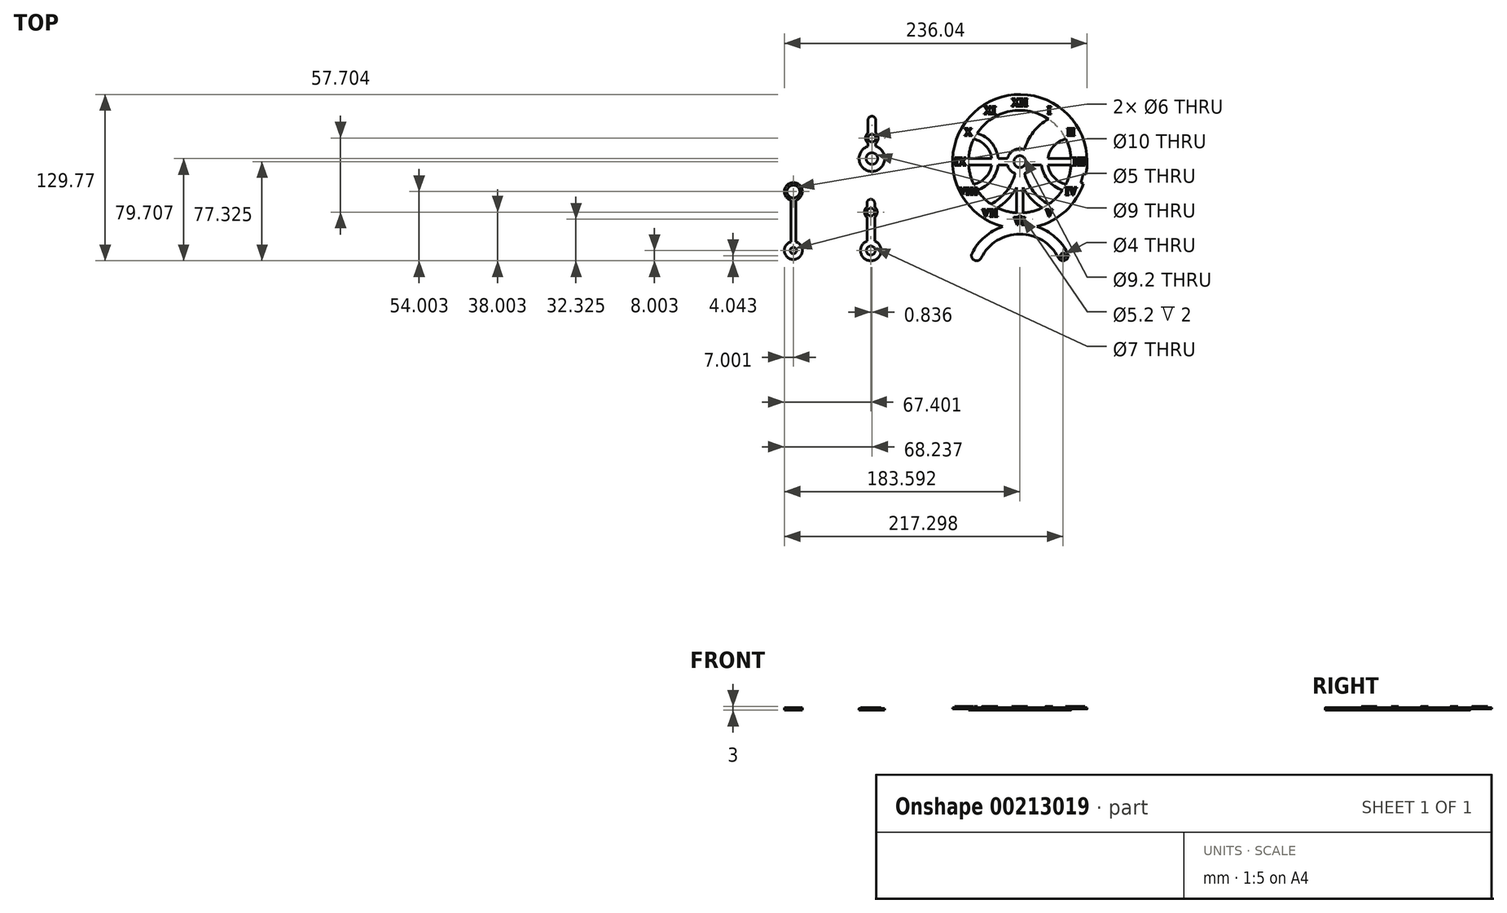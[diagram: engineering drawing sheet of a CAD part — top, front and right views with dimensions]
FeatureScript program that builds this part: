
annotation { "Feature Type Name" : "Feature", "Feature Type Description" : "" }
export const myFeature = defineFeature(function(context is Context, id is Id, definition is map)
    precondition{}
    {
        {
            var Q0;
            Q0=qCreatedBy(makeId("Top.planeOp"),FACE);
            var sketch = newSketch(context, id + "F0", { "sketchPlane" : qUnion([Q0])});
            skCircle(sketch, "E0", {"center": v(17.12, 18.95) * mm, "radius": 4.6 * mm});
            skCircle(sketch, "E1", {"center": v(17.12, -26.05) * mm, "radius": 2.6 * mm});
            skLineSegment(sketch, "E2", {"start": v(17.12, 18.95) * mm, "end": v(17.12, -26.05) * mm, "construction": true});
            skLineSegment(sketch, "E3", {"start": v(17.12, 18.95) * mm, "end": v(17.12, -34.39) * mm, "construction": true});
            skCircle(sketch, "E4", {"center": v(17.12, 18.95) * mm, "radius": 10 * mm});
            skLineSegment(sketch, "E5", {"start": v(-29.32, 18.95) * mm, "end": v(17.12, 18.95) * mm, "construction": true});
            skCircle(sketch, "E6", {"center": v(17.12, 18.95) * mm, "radius": 40 * mm});
            skArc(sketch, "E7", {"start": v(-25.5, -11.61) * mm, "mid": v(17.12, -71.05) * mm, "end": v(59.74, -11.61) * mm, "construction": true});
            skArc(sketch, "E8", {"start": v(-26.9, -9.57) * mm, "mid": v(17.12, -73.05) * mm, "end": v(61.14, -9.57) * mm, "construction": true});
            skArc(sketch, "E9", {"start": v(61.14, -9.57) * mm, "mid": v(17.12, 71.39) * mm, "end": v(-26.9, -9.57) * mm});
            skLineSegment(sketch, "E10", {"start": v(17.12, -26.05) * mm, "end": v(-13.24, -26.05) * mm, "construction": true});
            skLineSegment(sketch, "E11", {"start": v(17.12, 18.95) * mm, "end": v(17.12, 58.95) * mm, "construction": true});
            skLineSegment(sketch, "E12", {"start": v(17.12, 18.95) * mm, "end": v(37.12, 53.59) * mm, "construction": true});
            skLineSegment(sketch, "E13", {"start": v(17.12, 18.95) * mm, "end": v(51.76, 38.95) * mm, "construction": true});
            skLineSegment(sketch, "E14", {"start": v(17.12, 18.95) * mm, "end": v(57.12, 18.95) * mm, "construction": true});
            skLineSegment(sketch, "E15", {"start": v(17.12, 18.95) * mm, "end": v(51.76, -1.05) * mm, "construction": true});
            skLineSegment(sketch, "E16", {"start": v(17.12, 18.95) * mm, "end": v(37.12, -15.7) * mm, "construction": true});
            skCircle(sketch, "E17", {"center": v(57.12, 18.95) * mm, "radius": 40 * mm, "construction": true});
            skCircle(sketch, "E18", {"center": v(57.12, 18.95) * mm, "radius": 20.7 * mm, "construction": true});
            skArc(sketch, "E19", {"start": v(15.8, 28.86) * mm, "mid": v(17.39, 34.02) * mm, "end": v(19.62, 38.95) * mm, "construction": true});
            skArc(sketch, "E20", {"start": v(20.8, 28.25) * mm, "mid": v(27.65, 42.14) * mm, "end": v(39.54, 52.07) * mm});
            skArc(sketch, "E21", {"start": v(50.4, 41.15) * mm, "mid": v(39.26, 33.76) * mm, "end": v(34.05, 21.45) * mm});
            skArc(sketch, "E22", {"start": v(52.98, 36.67) * mm, "mid": v(43.67, 31.21) * mm, "end": v(39.09, 21.45) * mm});
            skArc(sketch, "E23", {"start": v(15.8, 9.03) * mm, "mid": v(17.39, 3.87) * mm, "end": v(19.62, -1.05) * mm, "construction": true});
            skArc(sketch, "E24", {"start": v(20.8, 9.64) * mm, "mid": v(27.65, -4.25) * mm, "end": v(39.54, -14.18) * mm});
            skLineSegment(sketch, "E25", {"start": v(26.8, 21.45) * mm, "end": v(34.05, 21.45) * mm});
            skLineSegment(sketch, "E26", {"start": v(26.8, 16.45) * mm, "end": v(34.05, 16.45) * mm});
            skLineSegment(sketch, "E27", {"start": v(14.62, 28.63) * mm, "end": v(14.62, 58.87) * mm, "construction": true});
            skLineSegment(sketch, "E28", {"start": v(19.62, 58.87) * mm, "end": v(19.62, 38.95) * mm});
            skLineSegment(sketch, "E29.MirrorCS", {"start": v(14.62, 9.26) * mm, "end": v(14.62, -20.98) * mm, "construction": true});
            skLineSegment(sketch, "E30.MirrorCS", {"start": v(19.62, -20.98) * mm, "end": v(19.62, -1.05) * mm});
            skArc(sketch, "E31", {"start": v(34.05, 21.45) * mm, "mid": v(33.92, 18.95) * mm, "end": v(34.05, 16.45) * mm, "construction": true});
            skArc(sketch, "E32", {"start": v(34.05, 16.45) * mm, "mid": v(39.26, 4.13) * mm, "end": v(50.4, -3.26) * mm});
            skLineSegment(sketch, "E33", {"start": v(34.05, 21.45) * mm, "end": v(39.09, 21.45) * mm, "construction": true});
            skLineSegment(sketch, "E34", {"start": v(39.09, 21.45) * mm, "end": v(57.04, 21.45) * mm});
            skLineSegment(sketch, "E35", {"start": v(34.05, 16.45) * mm, "end": v(39.09, 16.45) * mm, "construction": true});
            skLineSegment(sketch, "E36", {"start": v(39.09, 16.45) * mm, "end": v(57.04, 16.45) * mm});
            skArc(sketch, "E37", {"start": v(39.09, 16.45) * mm, "mid": v(43.67, 6.68) * mm, "end": v(52.98, 1.22) * mm});
            skArc(sketch, "E38", {"start": v(39.09, 21.45) * mm, "mid": v(38.92, 18.95) * mm, "end": v(39.09, 16.45) * mm, "construction": true});
            skArc(sketch, "E39", {"start": v(19.62, 38.95) * mm, "mid": v(26.04, 47.93) * mm, "end": v(34.54, 54.95) * mm});
            skArc(sketch, "E40", {"start": v(19.62, -1.05) * mm, "mid": v(26.04, -10.03) * mm, "end": v(34.54, -17.06) * mm});
            skLineSegment(sketch, "E41", {"start": v(19.62, -1.05) * mm, "end": v(19.62, 9.26) * mm, "construction": true});
            skLineSegment(sketch, "E42", {"start": v(19.62, 38.95) * mm, "end": v(19.62, 28.63) * mm, "construction": true});
            skLineSegment(sketch, "E43.MirrorCS", {"start": v(14.62, 58.87) * mm, "end": v(14.62, 38.95) * mm});
            skArc(sketch, "E44.MirrorCS", {"start": v(14.62, 38.95) * mm, "mid": v(8.2, 47.93) * mm, "end": v(-0.3, 54.95) * mm});
            skArc(sketch, "E45.MirrorCS", {"start": v(13.45, 28.25) * mm, "mid": v(6.6, 42.14) * mm, "end": v(-5.3, 52.07) * mm});
            skLineSegment(sketch, "E46.MirrorCS", {"start": v(7.44, 21.45) * mm, "end": v(0.2, 21.45) * mm});
            skLineSegment(sketch, "E47.MirrorCS", {"start": v(7.44, 16.45) * mm, "end": v(0.2, 16.45) * mm});
            skArc(sketch, "E48.MirrorCS", {"start": v(-16.15, 41.15) * mm, "mid": v(-5.01, 33.76) * mm, "end": v(0.2, 21.45) * mm});
            skArc(sketch, "E49.MirrorCS", {"start": v(-18.73, 36.67) * mm, "mid": v(-9.43, 31.21) * mm, "end": v(-4.84, 21.45) * mm});
            skArc(sketch, "E50.MirrorCS", {"start": v(0.2, 16.45) * mm, "mid": v(-5.01, 4.13) * mm, "end": v(-16.15, -3.26) * mm});
            skArc(sketch, "E51.MirrorCS", {"start": v(-4.84, 16.45) * mm, "mid": v(-9.43, 6.68) * mm, "end": v(-18.73, 1.22) * mm});
            skLineSegment(sketch, "E52.MirrorCS", {"start": v(-4.84, 16.45) * mm, "end": v(-22.8, 16.45) * mm});
            skLineSegment(sketch, "E53.MirrorCS", {"start": v(-4.84, 21.45) * mm, "end": v(-22.8, 21.45) * mm});
            skArc(sketch, "E54.MirrorCS", {"start": v(13.45, 9.64) * mm, "mid": v(6.6, -4.25) * mm, "end": v(-5.3, -14.18) * mm});
            skArc(sketch, "E55.MirrorCS", {"start": v(14.62, -1.05) * mm, "mid": v(8.2, -10.03) * mm, "end": v(-0.3, -17.06) * mm});
            skLineSegment(sketch, "E56.MirrorCS", {"start": v(14.62, -20.98) * mm, "end": v(14.62, -1.05) * mm});
            skArc(sketch, "E57", {"start": v(-26.9, -9.57) * mm, "mid": v(-13.69, -23.5) * mm, "end": v(3.65, -31.74) * mm});
            skArc(sketch, "E58", {"start": v(3.8, -31.78) * mm, "mid": v(17.2, -33.5) * mm, "end": v(30.6, -31.74) * mm, "construction": true});
            skArc(sketch, "E59", {"start": v(30.7, -31.71) * mm, "mid": v(47.97, -23.47) * mm, "end": v(61.14, -9.57) * mm});
            skLineSegment(sketch, "E60", {"start": v(17.12, -26.05) * mm, "end": v(-16.58, -54.34) * mm, "construction": true});
            skCircle(sketch, "E61", {"center": v(-16.58, -54.34) * mm, "radius": 2 * mm});
            skCircle(sketch, "E62.MirrorC", {"center": v(50.83, -54.34) * mm, "radius": 2 * mm});
            skCircle(sketch, "E63", {"center": v(17.12, -71.18) * mm, "radius": 37.68 * mm, "construction": true});
            skPoint(sketch, "E63.third.point", {"position": v(17.12, -33.5) * mm});
            skArc(sketch, "E64", {"start": v(-20.16, -52.55) * mm, "mid": v(17.12, -112.86) * mm, "end": v(54.4, -52.55) * mm, "construction": true});
            skArc(sketch, "E65", {"start": v(3.65, -31.74) * mm, "mid": v(-10.3, -39.8) * mm, "end": v(-20.16, -52.55) * mm});
            skArc(sketch, "E66", {"start": v(30.6, -31.74) * mm, "mid": v(17.12, -29.5) * mm, "end": v(3.65, -31.74) * mm, "construction": true});
            skArc(sketch, "E67", {"start": v(54.4, -52.55) * mm, "mid": v(44.55, -39.8) * mm, "end": v(30.6, -31.74) * mm});
            skArc(sketch, "E68", {"start": v(47.25, -56.13) * mm, "mid": v(17.12, -37.5) * mm, "end": v(-13, -56.13) * mm});
            skArc(sketch, "E69", {"start": v(-13, -56.13) * mm, "mid": v(17.12, -104.86) * mm, "end": v(47.25, -56.13) * mm, "construction": true});
            skArc(sketch, "E70", {"start": v(47.25, -56.13) * mm, "mid": v(52.62, -57.92) * mm, "end": v(54.4, -52.55) * mm});
            skArc(sketch, "E71", {"start": v(54.4, -52.55) * mm, "mid": v(49.04, -50.76) * mm, "end": v(47.25, -56.13) * mm, "construction": true});
            skArc(sketch, "E72", {"start": v(-20.16, -52.55) * mm, "mid": v(-18.37, -57.92) * mm, "end": v(-13, -56.13) * mm});
            skArc(sketch, "E73", {"start": v(-13, -56.13) * mm, "mid": v(-14.8, -50.76) * mm, "end": v(-20.16, -52.55) * mm, "construction": true});
            skArc(sketch, "E74", {"start": v(3.65, -31.74) * mm, "mid": v(3.73, -31.76) * mm, "end": v(3.8, -31.78) * mm, "construction": true});
            skArc(sketch, "E75", {"start": v(30.6, -31.74) * mm, "mid": v(30.65, -31.73) * mm, "end": v(30.7, -31.71) * mm});
            skCircle(sketch, "E76", {"center": v(17.12, 18.95) * mm, "radius": 46.22 * mm, "construction": true});
            skLineSegment(sketch, "E77", {"start": v(17.12, 58.95) * mm, "end": v(17.12, 65.17) * mm, "construction": true});
            skLineSegment(sketch, "E78", {"start": v(37.12, 53.59) * mm, "end": v(40.22, 58.95) * mm, "construction": true});
            skLineSegment(sketch, "E79", {"start": v(51.76, 38.95) * mm, "end": v(57.15, 42.06) * mm, "construction": true});
            skLineSegment(sketch, "E80", {"start": v(57.12, 18.95) * mm, "end": v(63.34, 18.95) * mm, "construction": true});
            skLineSegment(sketch, "E81", {"start": v(51.76, -1.05) * mm, "end": v(57.15, -4.17) * mm, "construction": true});
            skLineSegment(sketch, "E82", {"start": v(37.12, -15.7) * mm, "end": v(40.23, -21.08) * mm, "construction": true});
            skLineSegment(sketch, "E83.MirrorCS", {"start": v(-2.88, 53.59) * mm, "end": v(-5.97, 58.95) * mm, "construction": true});
            skLineSegment(sketch, "E84.MirrorCS", {"start": v(-17.52, 38.95) * mm, "end": v(-22.9, 42.06) * mm, "construction": true});
            skLineSegment(sketch, "E85.MirrorCS", {"start": v(-22.88, 18.95) * mm, "end": v(-29.1, 18.95) * mm, "construction": true});
            skLineSegment(sketch, "E86.MirrorCS", {"start": v(-17.52, -1.05) * mm, "end": v(-22.9, -4.17) * mm, "construction": true});
            skLineSegment(sketch, "E87.MirrorCS", {"start": v(-2.88, -15.7) * mm, "end": v(-5.99, -21.08) * mm, "construction": true});
            skPoint(sketch, "E88", {"position": v(17.12, -27.28) * mm});
            skCircle(sketch, "E89", {"center": v(-98.23, 21.33) * mm, "radius": 10 * mm});
            skCircle(sketch, "E90", {"center": v(-98.23, 21.33) * mm, "radius": 4.5 * mm});
            skLineSegment(sketch, "E91", {"start": v(-98.23, 21.33) * mm, "end": v(-98.23, 63.06) * mm, "construction": true});
            skLineSegment(sketch, "E92", {"start": v(-101.23, 51.33) * mm, "end": v(-101.23, 41.33) * mm});
            skLineSegment(sketch, "E93", {"start": v(-95.23, 51.33) * mm, "end": v(-95.23, 41.33) * mm});
            skArc(sketch, "E94", {"start": v(-101.23, 51.33) * mm, "mid": v(-98.23, 48.33) * mm, "end": v(-95.23, 51.33) * mm, "construction": true});
            skArc(sketch, "E95", {"start": v(-95.23, 51.33) * mm, "mid": v(-98.23, 54.33) * mm, "end": v(-101.23, 51.33) * mm});
            skCircle(sketch, "E96", {"center": v(-98.23, 37.33) * mm, "radius": 5 * mm});
            skLineSegment(sketch, "E97", {"start": v(-101.23, 41.33) * mm, "end": v(-101.23, 33.33) * mm, "construction": true});
            skLineSegment(sketch, "E98", {"start": v(-101.23, 33.33) * mm, "end": v(-101.23, 30.87) * mm});
            skLineSegment(sketch, "E99", {"start": v(-95.23, 33.33) * mm, "end": v(-95.23, 30.87) * mm});
            skLineSegment(sketch, "E100", {"start": v(-95.23, 41.33) * mm, "end": v(-95.23, 33.33) * mm, "construction": true});
            skCircle(sketch, "E101", {"center": v(-98.23, 37.33) * mm, "radius": 3 * mm});
            skCircle(sketch, "E102", {"center": v(-99.07, -50.38) * mm, "radius": 8 * mm});
            skCircle(sketch, "E103", {"center": v(-99.07, -50.38) * mm, "radius": 3.5 * mm});
            skLineSegment(sketch, "E104", {"start": v(-102.07, -13.38) * mm, "end": v(-102.07, -16.38) * mm});
            skLineSegment(sketch, "E105", {"start": v(-96.07, -13.38) * mm, "end": v(-96.07, -16.38) * mm});
            skArc(sketch, "E106", {"start": v(-102.07, -13.38) * mm, "mid": v(-99.07, -16.38) * mm, "end": v(-96.07, -13.38) * mm, "construction": true});
            skArc(sketch, "E107", {"start": v(-96.07, -13.38) * mm, "mid": v(-99.07, -10.38) * mm, "end": v(-102.07, -13.38) * mm});
            skCircle(sketch, "E108", {"center": v(-99.07, -20.38) * mm, "radius": 5 * mm});
            skLineSegment(sketch, "E109", {"start": v(-102.07, -16.38) * mm, "end": v(-102.07, -24.38) * mm, "construction": true});
            skLineSegment(sketch, "E110", {"start": v(-102.07, -24.38) * mm, "end": v(-102.07, -42.96) * mm});
            skLineSegment(sketch, "E111", {"start": v(-96.07, -24.38) * mm, "end": v(-96.07, -42.96) * mm});
            skLineSegment(sketch, "E112", {"start": v(-96.07, -16.38) * mm, "end": v(-96.07, -24.38) * mm, "construction": true});
            skCircle(sketch, "E113", {"center": v(-99.07, -20.38) * mm, "radius": 3 * mm});
            skCircle(sketch, "E114", {"center": v(-159.47, -50.38) * mm, "radius": 7 * mm});
            skCircle(sketch, "E115", {"center": v(-159.47, -50.38) * mm, "radius": 2.5 * mm});
            skCircle(sketch, "E116", {"center": v(-159.47, -4.38) * mm, "radius": 7 * mm});
            skLineSegment(sketch, "E117", {"start": v(-161.47, -11.09) * mm, "end": v(-161.47, -43.67) * mm});
            skLineSegment(sketch, "E118", {"start": v(-157.47, -11.09) * mm, "end": v(-157.47, -43.67) * mm});
            skCircle(sketch, "E119", {"center": v(-159.47, -4.38) * mm, "radius": 5 * mm});
            skLineSegment(sketch, "E120", {"start": v(-99.07, -50.38) * mm, "end": v(-99.07, -13.38) * mm, "construction": true});
            skLineSegment(sketch, "E121", {"start": v(-159.47, -50.38) * mm, "end": v(-159.47, -4.38) * mm, "construction": true});
            skLineSegment(sketch, "E122", {"start": v(17.12, 18.95) * mm, "end": v(-33.53, 5.37) * mm, "construction": true});
            skLineSegment(sketch, "E123", {"start": v(17.12, 18.95) * mm, "end": v(-32.2, 9.4) * mm, "construction": true});
            skArc(sketch, "E124", {"start": v(-32.2, 9.4) * mm, "mid": v(-31.4, 5.94) * mm, "end": v(-30.37, 2.55) * mm});
            skLineSegment(sketch, "E125", {"start": v(-32.2, 9.4) * mm, "end": v(-34.37, 8.98) * mm});
            skLineSegment(sketch, "E126", {"start": v(17.12, 18.95) * mm, "end": v(-30.37, 2.55) * mm, "construction": true});
            skLineSegment(sketch, "E127", {"start": v(-30.37, 2.55) * mm, "end": v(-32.45, 1.83) * mm});
            skLineSegment(sketch, "E128.1.0", {"start": v(-15.81, 56.89) * mm, "end": v(-17.25, 58.55) * mm});
            skArc(sketch, "E128.1.1", {"start": v(-15.81, 56.89) * mm, "mid": v(-18.4, 54.47) * mm, "end": v(-20.82, 51.88) * mm});
            skLineSegment(sketch, "E128.1.2", {"start": v(-20.82, 51.88) * mm, "end": v(-22.48, 53.32) * mm});
            skLineSegment(sketch, "E128.anchor1", {"start": v(17.12, 18.95) * mm, "end": v(-34.37, 8.98) * mm, "construction": true});
            skLineSegment(sketch, "E128.anchor2", {"start": v(17.12, 18.95) * mm, "end": v(-17.25, 58.55) * mm, "construction": true});
            skLineSegment(sketch, "E129.MirrorCS", {"start": v(50.06, 56.89) * mm, "end": v(51.5, 58.55) * mm});
            skLineSegment(sketch, "E130.MirrorCS", {"start": v(55.07, 51.88) * mm, "end": v(56.73, 53.32) * mm});
            skArc(sketch, "E131.MirrorCS", {"start": v(50.06, 56.89) * mm, "mid": v(52.65, 54.47) * mm, "end": v(55.07, 51.88) * mm});
            skArc(sketch, "E132.MirrorCS", {"start": v(66.45, 9.4) * mm, "mid": v(65.65, 5.94) * mm, "end": v(64.62, 2.55) * mm});
            skLineSegment(sketch, "E133.MirrorCS", {"start": v(64.62, 2.55) * mm, "end": v(66.7, 1.83) * mm});
            skLineSegment(sketch, "E134.MirrorCS", {"start": v(66.45, 9.4) * mm, "end": v(68.61, 8.98) * mm});
            skSolve(sketch);
        }
        {
            var Q0;
            Q0=makeQuery(id+"F0.imprint","IMPRINT",FACE,{"disambiguationData":[TD([[makeQuery(id+"F0.imprint","IMPRINT",EDGE,{"derivedFrom":sQuery(id+"F0.wireOp",EDGE,"46881f62-3ac5-47d6-aced-29528612543e")}),-1.0]])]});
            var Q1;
            {var subQ5=sQuery(id+"F0.wireOp",EDGE,"E46.MirrorCS");Q1=makeQuery(id+"F0.imprint","IMPRINT",FACE,{"disambiguationData":[TD([[makeQuery(id+"F0.imprint","IMPRINT",EDGE,{"derivedFrom":subQ5}),1.0]])]});}
            var Q2;
            {var subQ3=sQuery(id+"F0.wireOp",EDGE,"E20");Q2=makeQuery(id+"F0.imprint","IMPRINT",FACE,{"disambiguationData":[TD([[makeQuery(id+"F0.imprint","IMPRINT",EDGE,{"derivedFrom":subQ3}),1.0]])]});}
            var Q3;
            Q3=makeQuery(id+"F0.imprint","IMPRINT",FACE,{"disambiguationData":[TD([[makeQuery(id+"F0.imprint","IMPRINT",EDGE,{"derivedFrom":sQuery(id+"F0.wireOp",EDGE,"E0")}),-1.0]])]});
            var Q4;
            {var subQ4=sQuery(id+"F0.wireOp",EDGE,"E21");Q4=makeQuery(id+"F0.imprint","IMPRINT",FACE,{"disambiguationData":[TD([[makeQuery(id+"F0.imprint","IMPRINT",EDGE,{"derivedFrom":subQ4}),1.0]])]});}
            var Q5;
            {var subQ0=sQuery(id+"F0.wireOp",EDGE,"E24");Q5=makeQuery(id+"F0.imprint","IMPRINT",FACE,{"disambiguationData":[TD([[makeQuery(id+"F0.imprint","IMPRINT",EDGE,{"derivedFrom":subQ0}),-1.0]])]});}
            var Q6;
            Q6=makeQuery(id+"F0.imprint","IMPRINT",FACE,{"disambiguationData":[TD([[makeQuery(id+"F0.imprint","IMPRINT",EDGE,{"derivedFrom":sQuery(id+"F0.wireOp",EDGE,"46881f62-3ac5-47d6-aced-29528612543e")}),1.0]])]});
            var Q7;
            Q7=makeQuery(id+"F0.imprint","IMPRINT",FACE,{"disambiguationData":[TD([[makeQuery(id+"F0.imprint","IMPRINT",EDGE,{"derivedFrom":sQuery(id+"F0.wireOp",EDGE,"3b9f8738-e9cf-4245-bbe8-540d9008e639")}),1.0]])]});
            var Q8;
            Q8=makeQuery(id+"F0.imprint","IMPRINT",FACE,{"disambiguationData":[TD([[makeQuery(id+"F0.imprint","IMPRINT",EDGE,{"derivedFrom":sQuery(id+"F0.wireOp",EDGE,"e9bbff67-bd03-4606-8ff2-ee5b4f4e024b0.MirrorC")}),-1.0]])]});
            var Q9;
            Q9=makeQuery(id+"F0.imprint","IMPRINT",FACE,{"disambiguationData":[TD([[makeQuery(id+"F0.imprint","IMPRINT",EDGE,{"derivedFrom":sQuery(id+"F0.wireOp",EDGE,"373d9756-d84a-4345-9d80-ccd6daeb79da0.MirrorC")}),-1.0]])]});
            var Q10;
            Q10=makeQuery(id+"F0.imprint","IMPRINT",FACE,{"disambiguationData":[TD([[makeQuery(id+"F0.imprint","IMPRINT",EDGE,{"derivedFrom":sQuery(id+"F0.wireOp",EDGE,"2b842c07-6978-4730-a1d5-0e2b84ce1a1e")}),1.0]])]});
            var Q11;
            Q11=makeQuery(id+"F0.imprint","IMPRINT",FACE,{"disambiguationData":[TD([[makeQuery(id+"F0.imprint","IMPRINT",EDGE,{"derivedFrom":sQuery(id+"F0.wireOp",EDGE,"a3879617-aeb5-481f-b6d8-f8384f611423.MirrorC")}),-1.0]])]});
            var Q12;
            Q12=makeQuery(id+"F0.imprint","IMPRINT",FACE,{"disambiguationData":[TD([[makeQuery(id+"F0.imprint","IMPRINT",EDGE,{"derivedFrom":sQuery(id+"F0.wireOp",EDGE,"E61")}),1.0]])]});
            var Q13;
            Q13=makeQuery(id+"F0.imprint","IMPRINT",FACE,{"disambiguationData":[TD([[makeQuery(id+"F0.imprint","IMPRINT",EDGE,{"derivedFrom":sQuery(id+"F0.wireOp",EDGE,"E62.MirrorC")}),-1.0]])]});
            var Q14;
            Q14=makeQuery(id+"F0.imprint","IMPRINT",FACE,{"disambiguationData":[TD([[makeQuery(id+"F0.imprint","IMPRINT",EDGE,{"derivedFrom":sQuery(id+"F0.wireOp",EDGE,"E1")}),-1.0]])]});
            var Q15;
            Q15=makeQuery(id+"F0.imprint","IMPRINT",FACE,{"disambiguationData":[TD([[makeQuery(id+"F0.imprint","IMPRINT",EDGE,{"derivedFrom":sQuery(id+"F0.wireOp",EDGE,"E132.MirrorCS")}),1.0]])]});
            var Q16;
            {var subQ0=sQuery(id+"F0.wireOp",EDGE,"E129.MirrorCS");Q16=makeQuery(id+"F0.imprint","IMPRINT",FACE,{"disambiguationData":[TD([[makeQuery(id+"F0.imprint","IMPRINT",EDGE,{"derivedFrom":subQ0}),-1.0]])]});}
            var Q17;
            {var subQ0=sQuery(id+"F0.wireOp",EDGE,"E128.1.0");Q17=makeQuery(id+"F0.imprint","IMPRINT",FACE,{"disambiguationData":[TD([[makeQuery(id+"F0.imprint","IMPRINT",EDGE,{"derivedFrom":subQ0}),1.0]])]});}
            var Q18;
            Q18=makeQuery(id+"F0.imprint","IMPRINT",FACE,{"disambiguationData":[TD([[makeQuery(id+"F0.imprint","IMPRINT",EDGE,{"derivedFrom":sQuery(id+"F0.wireOp",EDGE,"E124")}),-1.0]])]});
            extrude(context, id + "F1", {"entities" : qUnion([Q0, Q1, Q2, Q3, Q4, Q5, Q6, Q7, Q8, Q9, Q10, Q11, Q12, Q13, Q14, Q15, Q16, Q17, Q18]), "depth" : 2 * mm});
        }
        {
            var Q0;
            Q0=makeQuery(id+"F0.imprint","IMPRINT",FACE,{"disambiguationData":[TD([[makeQuery(id+"F0.imprint","IMPRINT",EDGE,{"derivedFrom":sQuery(id+"F0.wireOp",EDGE,"a3879617-aeb5-481f-b6d8-f8384f611423.MirrorC")}),-1.0]])]});
            var Q1;
            Q1=makeQuery(id+"F0.imprint","IMPRINT",FACE,{"disambiguationData":[TD([[makeQuery(id+"F0.imprint","IMPRINT",EDGE,{"derivedFrom":sQuery(id+"F0.wireOp",EDGE,"2b842c07-6978-4730-a1d5-0e2b84ce1a1e")}),1.0]])]});
            var Q2;
            Q2=makeQuery(id+"F0.imprint","IMPRINT",FACE,{"disambiguationData":[TD([[makeQuery(id+"F0.imprint","IMPRINT",EDGE,{"derivedFrom":sQuery(id+"F0.wireOp",EDGE,"e9bbff67-bd03-4606-8ff2-ee5b4f4e024b0.MirrorC")}),-1.0]])]});
            var Q3;
            Q3=makeQuery(id+"F0.imprint","IMPRINT",FACE,{"disambiguationData":[TD([[makeQuery(id+"F0.imprint","IMPRINT",EDGE,{"derivedFrom":sQuery(id+"F0.wireOp",EDGE,"373d9756-d84a-4345-9d80-ccd6daeb79da0.MirrorC")}),-1.0]])]});
            var Q4;
            Q4=makeQuery(id+"F0.imprint","IMPRINT",FACE,{"disambiguationData":[TD([[makeQuery(id+"F0.imprint","IMPRINT",EDGE,{"derivedFrom":sQuery(id+"F0.wireOp",EDGE,"46881f62-3ac5-47d6-aced-29528612543e")}),1.0]])]});
            var Q5;
            Q5=makeQuery(id+"F0.imprint","IMPRINT",FACE,{"disambiguationData":[TD([[makeQuery(id+"F0.imprint","IMPRINT",EDGE,{"derivedFrom":sQuery(id+"F0.wireOp",EDGE,"3b9f8738-e9cf-4245-bbe8-540d9008e639")}),1.0]])]});
            var Q6;
            Q6=makeQuery(id+"F0.imprint","IMPRINT",FACE,{"disambiguationData":[TD([[makeQuery(id+"F0.imprint","IMPRINT",EDGE,{"derivedFrom":sQuery(id+"F0.wireOp",EDGE,"E62.MirrorC")}),-1.0]])]});
            var Q7;
            Q7=makeQuery(id+"F0.imprint","IMPRINT",FACE,{"disambiguationData":[TD([[makeQuery(id+"F0.imprint","IMPRINT",EDGE,{"derivedFrom":sQuery(id+"F0.wireOp",EDGE,"E61")}),1.0]])]});
            var Q8;
            Q8=makeQuery(id+"F0.imprint","IMPRINT",FACE,{"disambiguationData":[TD([[makeQuery(id+"F0.imprint","IMPRINT",EDGE,{"derivedFrom":sQuery(id+"F0.wireOp",EDGE,"E132.MirrorCS")}),1.0]])]});
            var Q9;
            {var subQ0=sQuery(id+"F0.wireOp",EDGE,"E129.MirrorCS");Q9=makeQuery(id+"F0.imprint","IMPRINT",FACE,{"disambiguationData":[TD([[makeQuery(id+"F0.imprint","IMPRINT",EDGE,{"derivedFrom":subQ0}),-1.0]])]});}
            var Q10;
            {var subQ0=sQuery(id+"F0.wireOp",EDGE,"E128.1.0");Q10=makeQuery(id+"F0.imprint","IMPRINT",FACE,{"disambiguationData":[TD([[makeQuery(id+"F0.imprint","IMPRINT",EDGE,{"derivedFrom":subQ0}),1.0]])]});}
            var Q11;
            Q11=makeQuery(id+"F0.imprint","IMPRINT",FACE,{"disambiguationData":[TD([[makeQuery(id+"F0.imprint","IMPRINT",EDGE,{"derivedFrom":sQuery(id+"F0.wireOp",EDGE,"E124")}),-1.0]])]});
            extrude(context, id + "F2", {"entities" : qUnion([Q0, Q1, Q2, Q3, Q4, Q5, Q6, Q7, Q8, Q9, Q10, Q11]), "operationType" : NewBodyOperationType.REMOVE, "depth" : 1 * mm});
        }
        {
            var Q0;
            Q0=makeQuery(id+"F1.opExtrude","CAP_FACE",FACE,{"disambiguationData":[OSD([sQuery(id+"F0.wireOp",EDGE,"E0"),sQuery(id+"F0.wireOp",EDGE,"E1"),sQuery(id+"F0.wireOp",EDGE,"E4"),sQuery(id+"F0.wireOp",EDGE,"E6"),sQuery(id+"F0.wireOp",EDGE,"E9"),sQuery(id+"F0.wireOp",EDGE,"E20"),sQuery(id+"F0.wireOp",EDGE,"E21"),sQuery(id+"F0.wireOp",EDGE,"E22"),sQuery(id+"F0.wireOp",EDGE,"E24"),sQuery(id+"F0.wireOp",EDGE,"E25"),sQuery(id+"F0.wireOp",EDGE,"E26"),sQuery(id+"F0.wireOp",EDGE,"E28"),sQuery(id+"F0.wireOp",EDGE,"E30.MirrorCS"),sQuery(id+"F0.wireOp",EDGE,"E32"),sQuery(id+"F0.wireOp",EDGE,"E34"),sQuery(id+"F0.wireOp",EDGE,"E36"),sQuery(id+"F0.wireOp",EDGE,"E37"),sQuery(id+"F0.wireOp",EDGE,"E39"),sQuery(id+"F0.wireOp",EDGE,"E40"),sQuery(id+"F0.wireOp",EDGE,"E43.MirrorCS"),sQuery(id+"F0.wireOp",EDGE,"E44.MirrorCS"),sQuery(id+"F0.wireOp",EDGE,"E45.MirrorCS"),sQuery(id+"F0.wireOp",EDGE,"E46.MirrorCS"),sQuery(id+"F0.wireOp",EDGE,"E47.MirrorCS"),sQuery(id+"F0.wireOp",EDGE,"E48.MirrorCS"),sQuery(id+"F0.wireOp",EDGE,"E49.MirrorCS"),sQuery(id+"F0.wireOp",EDGE,"E50.MirrorCS"),sQuery(id+"F0.wireOp",EDGE,"E51.MirrorCS"),sQuery(id+"F0.wireOp",EDGE,"E52.MirrorCS"),sQuery(id+"F0.wireOp",EDGE,"E53.MirrorCS"),sQuery(id+"F0.wireOp",EDGE,"E54.MirrorCS"),sQuery(id+"F0.wireOp",EDGE,"E55.MirrorCS"),sQuery(id+"F0.wireOp",EDGE,"E56.MirrorCS"),sQuery(id+"F0.wireOp",EDGE,"E57"),sQuery(id+"F0.wireOp",EDGE,"E59"),sQuery(id+"F0.wireOp",EDGE,"E65"),sQuery(id+"F0.wireOp",EDGE,"E67"),sQuery(id+"F0.wireOp",EDGE,"E68"),sQuery(id+"F0.wireOp",EDGE,"E70"),sQuery(id+"F0.wireOp",EDGE,"E72"),sQuery(id+"F0.wireOp",EDGE,"E75")])],"isStart":false});
            var sketch = newSketch(context, id + "F3", { "sketchPlane" : qUnion([Q0])});
            skText(sketch, "E135", { "text": "XII", "fontName": "NotoSerif-Bold.ttf"});
            skText(sketch, "E136", { "text": "I", "fontName": "NotoSerif-Bold.ttf"});
            skText(sketch, "E137", { "text": "II", "fontName": "NotoSerif-Bold.ttf"});
            skText(sketch, "E138", { "text": "III", "fontName": "NotoSerif-Bold.ttf"});
            skText(sketch, "E139", { "text": "IV", "fontName": "NotoSerif-Bold.ttf"});
            skText(sketch, "E140", { "text": "V", "fontName": "NotoSerif-Bold.ttf"});
            skText(sketch, "E141", { "text": "VI", "fontName": "NotoSerif-Bold.ttf"});
            skText(sketch, "E142", { "text": "VII", "fontName": "NotoSerif-Bold.ttf"});
            skText(sketch, "E143", { "text": "VIII", "fontName": "NotoSerif-Bold.ttf"});
            skText(sketch, "E144", { "text": "IX", "fontName": "NotoSerif-Bold.ttf"});
            skText(sketch, "E145", { "text": "X", "fontName": "NotoSerif-Bold.ttf"});
            skText(sketch, "E146", { "text": "XI", "fontName": "NotoSerif-Bold.ttf"});
            skLineSegment(sketch, "E147", {"start": v(38.76, 87.49) * mm, "end": v(38.76, 81.49) * mm});
            const initialGuessF3  = {"E135": [0.01058, 0.06217, 1, 0, 0.006], "E136": [0.0384, 0.05595, 1, 0, 0.006], "E137": [0.05366, 0.03906, 1, 0, 0.006], "E138": [0.05818, 0.01595, 1, 0, 0.006], "E139": [0.0523, -0.00717, 1, 0, 0.006], "E140": [0.03705, -0.02408, 1, 0, 0.006], "E141": [0.01239, -0.03028, 1, 0, 0.006], "E142": [-0.0124, -0.02408, 1, 0, 0.006], "E143": [-0.03044, -0.00697, 1, 0, 0.0056], "E144": [-0.03405, 0.01595, 1, 0, 0.006], "E145": [-0.02619, 0.03906, 1, 0, 0.006], "E146": [-0.01085, 0.05595, 1, 0, 0.006]};
            skSetInitialGuess(sketch, initialGuessF3);
            skSolve(sketch);
        }
        {
            var Q0;
            Q0=makeQuery(id+"F3.imprint","IMPRINT",FACE,{"disambiguationData":[TD([[makeQuery(id+"F3.imprint","IMPRINT",EDGE,{"derivedFrom":sQuery(id+"F3.wireOp",EDGE,"E135.sketch_text.stroke-0")}),-1.0]])]});
            var Q1;
            Q1=makeQuery(id+"F3.imprint","IMPRINT",FACE,{"disambiguationData":[TD([[makeQuery(id+"F3.imprint","IMPRINT",EDGE,{"derivedFrom":sQuery(id+"F3.wireOp",EDGE,"E135.sketch_text.stroke-27")}),-1.0]])]});
            var Q2;
            Q2=makeQuery(id+"F3.imprint","IMPRINT",FACE,{"disambiguationData":[TD([[makeQuery(id+"F3.imprint","IMPRINT",EDGE,{"derivedFrom":sQuery(id+"F3.wireOp",EDGE,"E136.sketch_text.stroke-0")}),-1.0]])]});
            var Q3;
            Q3=makeQuery(id+"F3.imprint","IMPRINT",FACE,{"disambiguationData":[TD([[makeQuery(id+"F3.imprint","IMPRINT",EDGE,{"derivedFrom":sQuery(id+"F3.wireOp",EDGE,"E137.sketch_text.stroke-0")}),-1.0]])]});
            var Q4;
            Q4=makeQuery(id+"F3.imprint","IMPRINT",FACE,{"disambiguationData":[TD([[makeQuery(id+"F3.imprint","IMPRINT",EDGE,{"derivedFrom":sQuery(id+"F3.wireOp",EDGE,"E138.sketch_text.stroke-0")}),-1.0]])]});
            var Q5;
            Q5=makeQuery(id+"F3.imprint","IMPRINT",FACE,{"disambiguationData":[TD([[makeQuery(id+"F3.imprint","IMPRINT",EDGE,{"derivedFrom":sQuery(id+"F3.wireOp",EDGE,"E139.sketch_text.stroke-0")}),-1.0]])]});
            var Q6;
            Q6=makeQuery(id+"F3.imprint","IMPRINT",FACE,{"disambiguationData":[TD([[makeQuery(id+"F3.imprint","IMPRINT",EDGE,{"derivedFrom":sQuery(id+"F3.wireOp",EDGE,"E140.sketch_text.stroke-0")}),-1.0]])]});
            var Q7;
            {var subQ11=sQuery(id+"F3.wireOp",EDGE,"E141.sketch_text.stroke-9");Q7=makeQuery(id+"F3.imprint","IMPRINT",FACE,{"disambiguationData":[TD([[makeQuery(id+"F3.imprint","IMPRINT",EDGE,{"derivedFrom":subQ11}),-1.0]])]});}
            var Q8;
            Q8=makeQuery(id+"F3.imprint","IMPRINT",FACE,{"disambiguationData":[TD([[makeQuery(id+"F3.imprint","IMPRINT",EDGE,{"derivedFrom":sQuery(id+"F3.wireOp",EDGE,"E141.sketch_text.stroke-0")}),-1.0]])]});
            var Q9;
            Q9=makeQuery(id+"F3.imprint","IMPRINT",FACE,{"disambiguationData":[TD([[makeQuery(id+"F3.imprint","IMPRINT",EDGE,{"derivedFrom":sQuery(id+"F3.wireOp",EDGE,"E142.sketch_text.stroke-0")}),-1.0]])]});
            var Q10;
            Q10=makeQuery(id+"F3.imprint","IMPRINT",FACE,{"disambiguationData":[TD([[makeQuery(id+"F3.imprint","IMPRINT",EDGE,{"derivedFrom":sQuery(id+"F3.wireOp",EDGE,"E143.sketch_text.stroke-0")}),-1.0]])]});
            var Q11;
            Q11=makeQuery(id+"F3.imprint","IMPRINT",FACE,{"disambiguationData":[TD([[makeQuery(id+"F3.imprint","IMPRINT",EDGE,{"derivedFrom":sQuery(id+"F3.wireOp",EDGE,"E144.sketch_text.stroke-0")}),-1.0]])]});
            var Q12;
            Q12=makeQuery(id+"F3.imprint","IMPRINT",FACE,{"disambiguationData":[TD([[makeQuery(id+"F3.imprint","IMPRINT",EDGE,{"derivedFrom":sQuery(id+"F3.wireOp",EDGE,"E145.sketch_text.stroke-0")}),-1.0]])]});
            var Q13;
            Q13=makeQuery(id+"F3.imprint","IMPRINT",FACE,{"disambiguationData":[TD([[makeQuery(id+"F3.imprint","IMPRINT",EDGE,{"derivedFrom":sQuery(id+"F3.wireOp",EDGE,"E145.sketch_text.stroke-27")}),-1.0]])]});
            var Q14;
            Q14=makeQuery(id+"F3.imprint","IMPRINT",FACE,{"disambiguationData":[TD([[makeQuery(id+"F3.imprint","IMPRINT",EDGE,{"derivedFrom":sQuery(id+"F3.wireOp",EDGE,"E146.sketch_text.stroke-0")}),-1.0]])]});
            var Q15;
            Q15=makeQuery(id+"F3.imprint","IMPRINT",FACE,{"disambiguationData":[TD([[makeQuery(id+"F3.imprint","IMPRINT",EDGE,{"derivedFrom":sQuery(id+"F3.wireOp",EDGE,"E146.sketch_text.stroke-27")}),-1.0]])]});
            var Q16;
            {var subQ1=sQuery(id+"F3.wireOp",EDGE,"E141.sketch_text.stroke-13");Q16=makeQuery(id+"F3.imprint","IMPRINT",FACE,{"disambiguationData":[TD([[makeQuery(id+"F3.imprint","IMPRINT",EDGE,{"derivedFrom":subQ1}),-1.0]])]});}
            var Q17;
            {var subQ4=sQuery(id+"F3.wireOp",EDGE,"E141.sketch_text.stroke-34");Q17=makeQuery(id+"F3.imprint","IMPRINT",FACE,{"disambiguationData":[TD([[makeQuery(id+"F3.imprint","IMPRINT",EDGE,{"derivedFrom":subQ4}),-1.0]])]});}
            var Q18;
            Q18=makeQuery(id+"F3.imprint","IMPRINT",FACE,{"disambiguationData":[TD([[makeQuery(id+"F3.imprint","IMPRINT",EDGE,{"derivedFrom":sQuery(id+"F3.wireOp",EDGE,"E141.sketch_text.stroke-31")}),-1.0]])]});
            var Q19;
            Q19=makeQuery(id+"F3.imprint","IMPRINT",FACE,{"disambiguationData":[TD([[makeQuery(id+"F3.imprint","IMPRINT",EDGE,{"derivedFrom":sQuery(id+"F3.wireOp",EDGE,"E145.sketch_text.stroke-7")}),-1.0]])]});
            var Q20;
            Q20=makeQuery(id+"F3.imprint","IMPRINT",FACE,{"disambiguationData":[TD([[makeQuery(id+"F3.imprint","IMPRINT",EDGE,{"derivedFrom":sQuery(id+"F3.wireOp",EDGE,"E144.sketch_text.stroke-14")}),-1.0]])]});
            var Q21;
            Q21=makeQuery(id+"F3.imprint","IMPRINT",FACE,{"disambiguationData":[TD([[makeQuery(id+"F3.imprint","IMPRINT",EDGE,{"derivedFrom":sQuery(id+"F3.wireOp",EDGE,"E146.sketch_text.stroke-7")}),-1.0]])]});
            var Q22;
            Q22=makeQuery(id+"F3.imprint","IMPRINT",FACE,{"disambiguationData":[TD([[makeQuery(id+"F3.imprint","IMPRINT",EDGE,{"derivedFrom":sQuery(id+"F3.wireOp",EDGE,"E135.sketch_text.stroke-7")}),-1.0]])]});
            var Q23;
            Q23=makeQuery(id+"F3.imprint","IMPRINT",FACE,{"disambiguationData":[TD([[makeQuery(id+"F3.imprint","IMPRINT",EDGE,{"derivedFrom":sQuery(id+"F3.wireOp",EDGE,"E135.sketch_text.stroke-14")}),-1.0]])]});
            var Q24;
            Q24=makeQuery(id+"F3.imprint","IMPRINT",FACE,{"disambiguationData":[TD([[makeQuery(id+"F3.imprint","IMPRINT",EDGE,{"derivedFrom":sQuery(id+"F3.wireOp",EDGE,"E135.sketch_text.stroke-18")}),-1.0]])]});
            var Q25;
            Q25=makeQuery(id+"F3.imprint","IMPRINT",FACE,{"disambiguationData":[TD([[makeQuery(id+"F3.imprint","IMPRINT",EDGE,{"derivedFrom":sQuery(id+"F3.wireOp",EDGE,"E137.sketch_text.stroke-4")}),-1.0]])]});
            var Q26;
            Q26=makeQuery(id+"F3.imprint","IMPRINT",FACE,{"disambiguationData":[TD([[makeQuery(id+"F3.imprint","IMPRINT",EDGE,{"derivedFrom":sQuery(id+"F3.wireOp",EDGE,"E138.sketch_text.stroke-4")}),-1.0]])]});
            var Q27;
            Q27=makeQuery(id+"F3.imprint","IMPRINT",FACE,{"disambiguationData":[TD([[makeQuery(id+"F3.imprint","IMPRINT",EDGE,{"derivedFrom":sQuery(id+"F3.wireOp",EDGE,"E138.sketch_text.stroke-8")}),-1.0]])]});
            var Q28;
            Q28=makeQuery(id+"F3.imprint","IMPRINT",FACE,{"disambiguationData":[TD([[makeQuery(id+"F3.imprint","IMPRINT",EDGE,{"derivedFrom":sQuery(id+"F3.wireOp",EDGE,"E139.sketch_text.stroke-4")}),-1.0]])]});
            var Q29;
            Q29=makeQuery(id+"F3.imprint","IMPRINT",FACE,{"disambiguationData":[TD([[makeQuery(id+"F3.imprint","IMPRINT",EDGE,{"derivedFrom":sQuery(id+"F3.wireOp",EDGE,"E139.sketch_text.stroke-9")}),-1.0]])]});
            var Q30;
            Q30=makeQuery(id+"F3.imprint","IMPRINT",FACE,{"disambiguationData":[TD([[makeQuery(id+"F3.imprint","IMPRINT",EDGE,{"derivedFrom":sQuery(id+"F3.wireOp",EDGE,"E140.sketch_text.stroke-5")}),-1.0]])]});
            var Q31;
            Q31=makeQuery(id+"F3.imprint","IMPRINT",FACE,{"disambiguationData":[TD([[makeQuery(id+"F3.imprint","IMPRINT",EDGE,{"derivedFrom":sQuery(id+"F3.wireOp",EDGE,"E142.sketch_text.stroke-5")}),-1.0]])]});
            var Q32;
            Q32=makeQuery(id+"F3.imprint","IMPRINT",FACE,{"disambiguationData":[TD([[makeQuery(id+"F3.imprint","IMPRINT",EDGE,{"derivedFrom":sQuery(id+"F3.wireOp",EDGE,"E142.sketch_text.stroke-10")}),-1.0]])]});
            var Q33;
            Q33=makeQuery(id+"F3.imprint","IMPRINT",FACE,{"disambiguationData":[TD([[makeQuery(id+"F3.imprint","IMPRINT",EDGE,{"derivedFrom":sQuery(id+"F3.wireOp",EDGE,"E142.sketch_text.stroke-14")}),-1.0]])]});
            var Q34;
            Q34=makeQuery(id+"F3.imprint","IMPRINT",FACE,{"disambiguationData":[TD([[makeQuery(id+"F3.imprint","IMPRINT",EDGE,{"derivedFrom":sQuery(id+"F3.wireOp",EDGE,"E143.sketch_text.stroke-5")}),-1.0]])]});
            var Q35;
            Q35=makeQuery(id+"F3.imprint","IMPRINT",FACE,{"disambiguationData":[TD([[makeQuery(id+"F3.imprint","IMPRINT",EDGE,{"derivedFrom":sQuery(id+"F3.wireOp",EDGE,"E143.sketch_text.stroke-10")}),-1.0]])]});
            var Q36;
            Q36=makeQuery(id+"F3.imprint","IMPRINT",FACE,{"disambiguationData":[TD([[makeQuery(id+"F3.imprint","IMPRINT",EDGE,{"derivedFrom":sQuery(id+"F3.wireOp",EDGE,"E143.sketch_text.stroke-14")}),-1.0]])]});
            var Q37;
            Q37=makeQuery(id+"F3.imprint","IMPRINT",FACE,{"disambiguationData":[TD([[makeQuery(id+"F3.imprint","IMPRINT",EDGE,{"derivedFrom":sQuery(id+"F3.wireOp",EDGE,"E143.sketch_text.stroke-18")}),-1.0]])]});
            var Q38;
            Q38=makeQuery(id+"F3.imprint","IMPRINT",FACE,{"disambiguationData":[TD([[makeQuery(id+"F3.imprint","IMPRINT",EDGE,{"derivedFrom":sQuery(id+"F3.wireOp",EDGE,"E144.sketch_text.stroke-4")}),-1.0]])]});
            var Q39;
            Q39=makeQuery(id+"F3.imprint","IMPRINT",FACE,{"disambiguationData":[TD([[makeQuery(id+"F3.imprint","IMPRINT",EDGE,{"derivedFrom":sQuery(id+"F3.wireOp",EDGE,"E146.sketch_text.stroke-14")}),-1.0]])]});
            var Q40;
            Q40=makeQuery(id+"F3.imprint","IMPRINT",FACE,{"disambiguationData":[TD([[makeQuery(id+"F3.imprint","IMPRINT",EDGE,{"derivedFrom":sQuery(id+"F3.wireOp",EDGE,"E138.sketch_text.stroke-28")}),-1.0]])]});
            var Q41;
            Q41=makeQuery(id+"F3.imprint","IMPRINT",FACE,{"disambiguationData":[TD([[makeQuery(id+"F3.imprint","IMPRINT",EDGE,{"derivedFrom":sQuery(id+"F3.wireOp",EDGE,"E138.sketch_text.stroke-56")}),-1.0]])]});
            var Q42;
            Q42=makeQuery(id+"F3.imprint","IMPRINT",FACE,{"disambiguationData":[TD([[makeQuery(id+"F3.imprint","IMPRINT",EDGE,{"derivedFrom":sQuery(id+"F3.wireOp",EDGE,"E135.sketch_text.stroke-65")}),-1.0]])]});
            var Q43;
            Q43=makeQuery(id+"F3.imprint","IMPRINT",FACE,{"disambiguationData":[TD([[makeQuery(id+"F3.imprint","IMPRINT",EDGE,{"derivedFrom":sQuery(id+"F3.wireOp",EDGE,"E135.sketch_text.stroke-93")}),-1.0]])]});
            var Q44;
            Q44=makeQuery(id+"F3.imprint","IMPRINT",FACE,{"disambiguationData":[TD([[makeQuery(id+"F3.imprint","IMPRINT",EDGE,{"derivedFrom":sQuery(id+"F3.wireOp",EDGE,"E137.sketch_text.stroke-28")}),-1.0]])]});
            var Q45;
            Q45=makeQuery(id+"F3.imprint","IMPRINT",FACE,{"disambiguationData":[TD([[makeQuery(id+"F3.imprint","IMPRINT",EDGE,{"derivedFrom":sQuery(id+"F3.wireOp",EDGE,"E139.sketch_text.stroke-28")}),-1.0]])]});
            var Q46;
            Q46=makeQuery(id+"F3.imprint","IMPRINT",FACE,{"disambiguationData":[TD([[makeQuery(id+"F3.imprint","IMPRINT",EDGE,{"derivedFrom":sQuery(id+"F3.wireOp",EDGE,"E141.sketch_text.stroke-35")}),-1.0]])]});
            var Q47;
            {var subQ5=sQuery(id+"F3.wireOp",EDGE,"E141.sketch_text.stroke-42");Q47=makeQuery(id+"F3.imprint","IMPRINT",FACE,{"disambiguationData":[TD([[makeQuery(id+"F3.imprint","IMPRINT",EDGE,{"derivedFrom":subQ5}),-1.0]])]});}
            var Q48;
            {var subQ0=sQuery(id+"F3.wireOp",EDGE,"E141.sketch_text.stroke-14");var subQ1=makeQuery(id+"F1.opExtrude","CAP_EDGE",EDGE,{"disambiguationData":[OSD([sQuery(id+"F0.wireOp",EDGE,"E1")])],"isStart":false});var subQ2=makeQuery(id+"F3.imprint","INTERSECT",VERTEX,{"disambiguationData":[OD(0.0)],"derivedFrom":[subQ1,subQ0]});Q48=makeQuery(id+"F3.imprint","IMPRINT",FACE,{"disambiguationData":[TD([[makeQuery(id+"F3.imprint","IMPRINT",EDGE,{"disambiguationData":[TD([[subQ2,-1.0]])],"derivedFrom":subQ0}),-1.0]])]});}
            var Q49;
            Q49=makeQuery(id+"F3.imprint","IMPRINT",FACE,{"disambiguationData":[TD([[makeQuery(id+"F3.imprint","IMPRINT",EDGE,{"derivedFrom":sQuery(id+"F3.wireOp",EDGE,"E142.sketch_text.stroke-35")}),-1.0]])]});
            var Q50;
            Q50=makeQuery(id+"F3.imprint","IMPRINT",FACE,{"disambiguationData":[TD([[makeQuery(id+"F3.imprint","IMPRINT",EDGE,{"derivedFrom":sQuery(id+"F3.wireOp",EDGE,"E142.sketch_text.stroke-63")}),-1.0]])]});
            var Q51;
            Q51=makeQuery(id+"F3.imprint","IMPRINT",FACE,{"disambiguationData":[TD([[makeQuery(id+"F3.imprint","IMPRINT",EDGE,{"derivedFrom":sQuery(id+"F3.wireOp",EDGE,"E143.sketch_text.stroke-35")}),-1.0]])]});
            var Q52;
            Q52=makeQuery(id+"F3.imprint","IMPRINT",FACE,{"disambiguationData":[TD([[makeQuery(id+"F3.imprint","IMPRINT",EDGE,{"derivedFrom":sQuery(id+"F3.wireOp",EDGE,"E143.sketch_text.stroke-63")}),-1.0]])]});
            var Q53;
            Q53=makeQuery(id+"F3.imprint","IMPRINT",FACE,{"disambiguationData":[TD([[makeQuery(id+"F3.imprint","IMPRINT",EDGE,{"derivedFrom":sQuery(id+"F3.wireOp",EDGE,"E143.sketch_text.stroke-91")}),-1.0]])]});
            var Q54;
            Q54=makeQuery(id+"F3.imprint","IMPRINT",FACE,{"disambiguationData":[TD([[makeQuery(id+"F3.imprint","IMPRINT",EDGE,{"derivedFrom":sQuery(id+"F3.wireOp",EDGE,"E144.sketch_text.stroke-28")}),-1.0]])]});
            var Q55;
            Q55=makeQuery(id+"F3.imprint","IMPRINT",FACE,{"disambiguationData":[TD([[makeQuery(id+"F3.imprint","IMPRINT",EDGE,{"derivedFrom":sQuery(id+"F3.wireOp",EDGE,"E146.sketch_text.stroke-65")}),-1.0]])]});
            var Q56;
            Q56=makeQuery(id+"F3.imprint","IMPRINT",FACE,{"disambiguationData":[TD([[makeQuery(id+"F3.imprint","IMPRINT",EDGE,{"derivedFrom":sQuery(id+"F3.wireOp",EDGE,"E141.sketch_text.stroke-43")}),-1.0]])]});
            var Q57;
            {var subQ5=sQuery(id+"F3.wireOp",EDGE,"E141.sketch_text.stroke-50");Q57=makeQuery(id+"F3.imprint","IMPRINT",FACE,{"disambiguationData":[TD([[makeQuery(id+"F3.imprint","IMPRINT",EDGE,{"derivedFrom":subQ5}),-1.0]])]});}
            var Q58;
            Q58=makeQuery(id+"F3.imprint","IMPRINT",FACE,{"disambiguationData":[TD([[makeQuery(id+"F3.imprint","IMPRINT",EDGE,{"derivedFrom":sQuery(id+"F3.wireOp",EDGE,"E143.sketch_text.stroke-99")}),-1.0]])]});
            var Q59;
            Q59=makeQuery(id+"F3.imprint","IMPRINT",FACE,{"disambiguationData":[TD([[makeQuery(id+"F3.imprint","IMPRINT",EDGE,{"derivedFrom":sQuery(id+"F3.wireOp",EDGE,"E142.sketch_text.stroke-71")}),-1.0]])]});
            extrude(context, id + "F4", {"entities" : qUnion([Q0, Q1, Q2, Q3, Q4, Q5, Q6, Q7, Q8, Q9, Q10, Q11, Q12, Q13, Q14, Q15, Q16, Q17, Q18, Q19, Q20, Q21, Q22, Q23, Q24, Q25, Q26, Q27, Q28, Q29, Q30, Q31, Q32, Q33, Q34, Q35, Q36, Q37, Q38, Q39, Q40, Q41, Q42, Q43, Q44, Q45, Q46, Q47, Q48, Q49, Q50, Q51, Q52, Q53, Q54, Q55, Q56, Q57, Q58, Q59]), "operationType" : NewBodyOperationType.ADD, "depth" : 1 * mm});
        }
        {
            var Q0;
            Q0=makeQuery(id+"F0.imprint","IMPRINT",FACE,{"disambiguationData":[TD([[makeQuery(id+"F0.imprint","IMPRINT",EDGE,{"derivedFrom":sQuery(id+"F0.wireOp",EDGE,"E90")}),-1.0]])]});
            var Q1;
            {var subQ0=sQuery(id+"F0.wireOp",EDGE,"E98");Q1=makeQuery(id+"F0.imprint","IMPRINT",FACE,{"disambiguationData":[TD([[makeQuery(id+"F0.imprint","IMPRINT",EDGE,{"derivedFrom":subQ0}),1.0]])]});}
            var Q2;
            Q2=makeQuery(id+"F0.imprint","IMPRINT",FACE,{"disambiguationData":[TD([[makeQuery(id+"F0.imprint","IMPRINT",EDGE,{"derivedFrom":sQuery(id+"F0.wireOp",EDGE,"E101")}),-1.0]])]});
            var Q3;
            {var subQ0=sQuery(id+"F0.wireOp",EDGE,"E92");Q3=makeQuery(id+"F0.imprint","IMPRINT",FACE,{"disambiguationData":[TD([[makeQuery(id+"F0.imprint","IMPRINT",EDGE,{"derivedFrom":subQ0}),1.0]])]});}
            extrude(context, id + "F5", {"entities" : qUnion([Q0, Q1, Q2, Q3]), "depth" : 1.5 * mm});
        }
        {
            var Q0;
            Q0=makeQuery(id+"F0.imprint","IMPRINT",FACE,{"disambiguationData":[TD([[makeQuery(id+"F0.imprint","IMPRINT",EDGE,{"derivedFrom":sQuery(id+"F0.wireOp",EDGE,"E103")}),-1.0]])]});
            var Q1;
            {var subQ0=sQuery(id+"F0.wireOp",EDGE,"E110");Q1=makeQuery(id+"F0.imprint","IMPRINT",FACE,{"disambiguationData":[TD([[makeQuery(id+"F0.imprint","IMPRINT",EDGE,{"derivedFrom":subQ0}),1.0]])]});}
            var Q2;
            Q2=makeQuery(id+"F0.imprint","IMPRINT",FACE,{"disambiguationData":[TD([[makeQuery(id+"F0.imprint","IMPRINT",EDGE,{"derivedFrom":sQuery(id+"F0.wireOp",EDGE,"E113")}),-1.0]])]});
            var Q3;
            {var subQ0=sQuery(id+"F0.wireOp",EDGE,"E104");Q3=makeQuery(id+"F0.imprint","IMPRINT",FACE,{"disambiguationData":[TD([[makeQuery(id+"F0.imprint","IMPRINT",EDGE,{"derivedFrom":subQ0}),1.0]])]});}
            var Q4;
            Q4=makeQuery(id+"F0.imprint","IMPRINT",FACE,{"disambiguationData":[TD([[makeQuery(id+"F0.imprint","IMPRINT",EDGE,{"derivedFrom":sQuery(id+"F0.wireOp",EDGE,"E119")}),-1.0]])]});
            var Q5;
            {var subQ0=sQuery(id+"F0.wireOp",EDGE,"E117");Q5=makeQuery(id+"F0.imprint","IMPRINT",FACE,{"disambiguationData":[TD([[makeQuery(id+"F0.imprint","IMPRINT",EDGE,{"derivedFrom":subQ0}),1.0]])]});}
            var Q6;
            Q6=makeQuery(id+"F0.imprint","IMPRINT",FACE,{"disambiguationData":[TD([[makeQuery(id+"F0.imprint","IMPRINT",EDGE,{"derivedFrom":sQuery(id+"F0.wireOp",EDGE,"E115")}),-1.0]])]});
            extrude(context, id + "F6", {"entities" : qUnion([Q0, Q1, Q2, Q3, Q4, Q5, Q6]), "depth" : 2 * mm});
        }
    });
